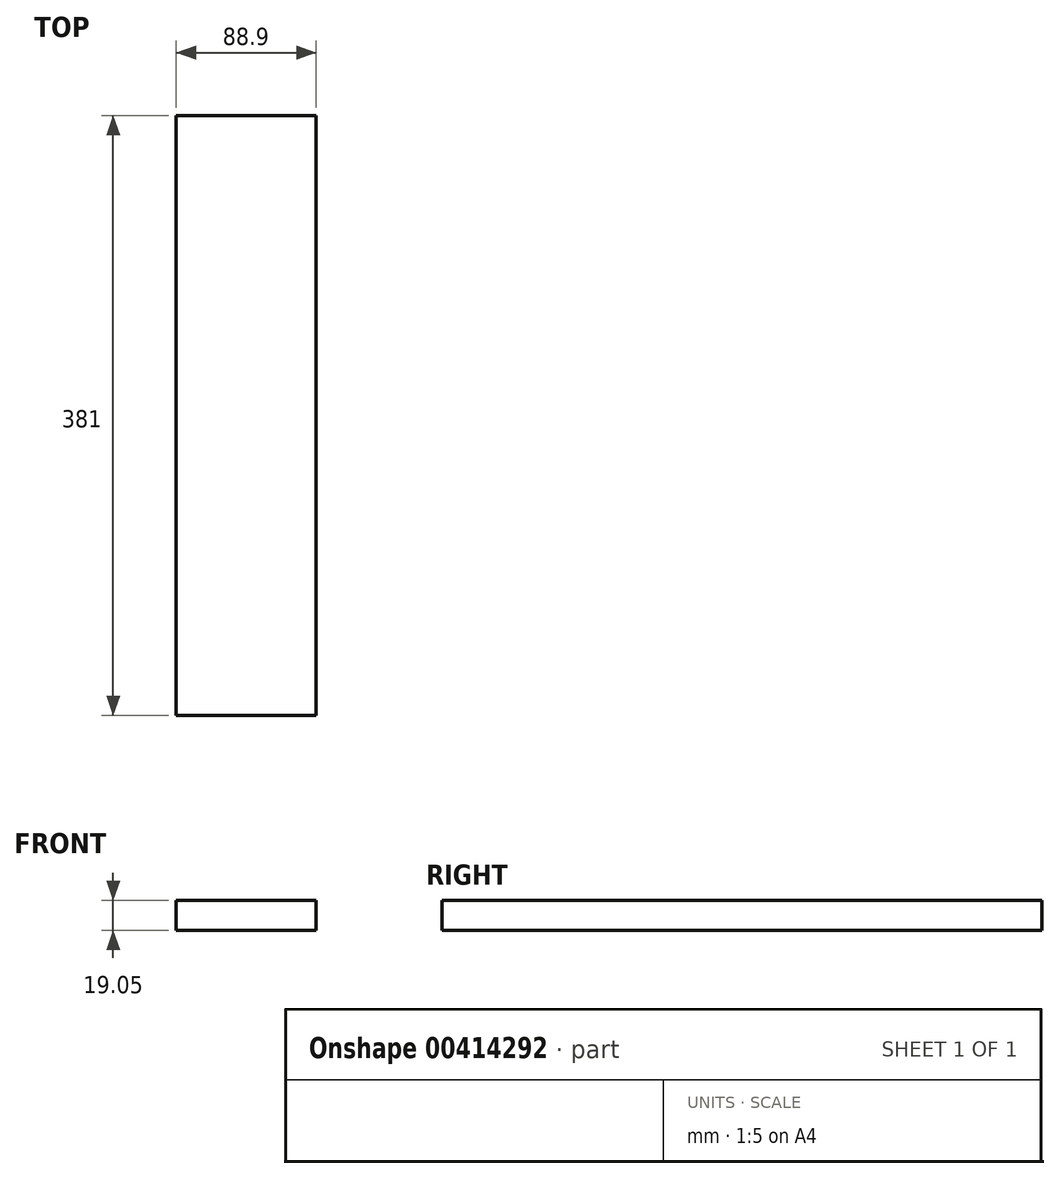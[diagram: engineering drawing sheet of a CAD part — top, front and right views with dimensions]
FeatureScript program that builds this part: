
annotation { "Feature Type Name" : "Feature", "Feature Type Description" : "" }
export const myFeature = defineFeature(function(context is Context, id is Id, definition is map)
    precondition{}
    {
        {
            var Q0;
            Q0=qCreatedBy(makeId("Front.planeOp"),FACE);
            var sketch = newSketch(context, id + "F0", { "sketchPlane" : qUnion([Q0])});
            skLineSegment(sketch, "E0.bottom", {"start": v(0, 0) * mm, "end": v(-88.9, 0) * mm});
            skLineSegment(sketch, "E0.top", {"start": v(0, 19.05) * mm, "end": v(-88.9, 19.05) * mm});
            skLineSegment(sketch, "E0.left", {"start": v(0, 0) * mm, "end": v(0, 19.05) * mm});
            skLineSegment(sketch, "E0.right", {"start": v(-88.9, 0) * mm, "end": v(-88.9, 19.05) * mm});
            skSolve(sketch);
        }
        {
            var Q0;
            Q0=qSketchRegion(id+"F0",true);
            extrude(context, id + "F1", {"entities" : qUnion([Q0]), "depth" : 381 * mm});
        }
    });
